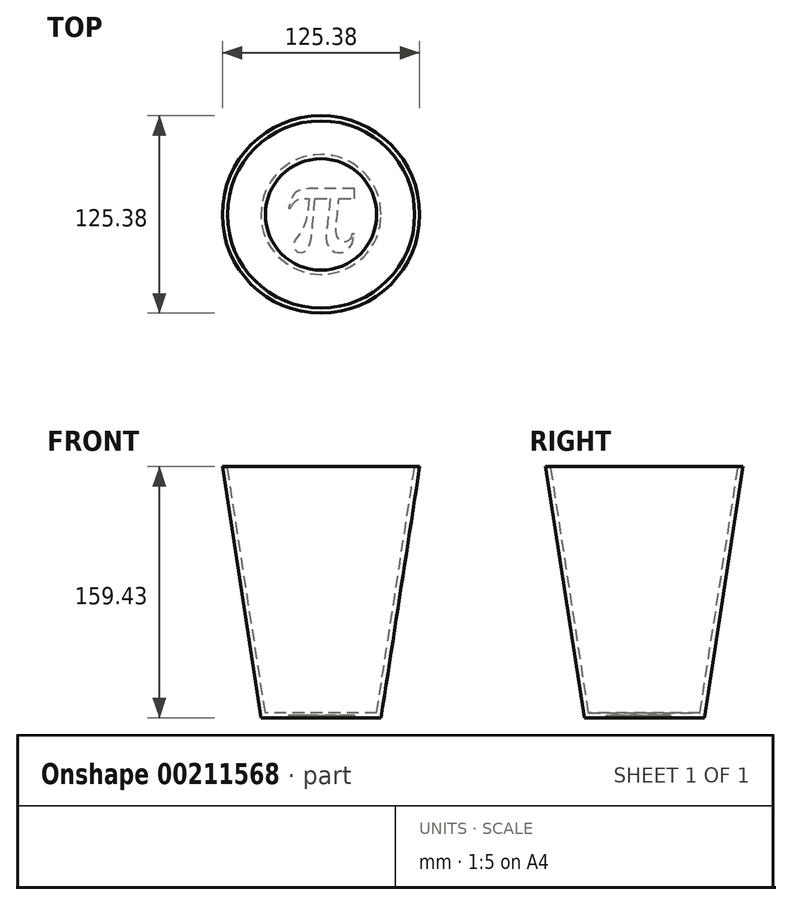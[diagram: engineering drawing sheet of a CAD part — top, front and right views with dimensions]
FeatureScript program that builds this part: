
annotation { "Feature Type Name" : "Feature", "Feature Type Description" : "" }
export const myFeature = defineFeature(function(context is Context, id is Id, definition is map)
    precondition{}
    {
        {
            var Q0;
            Q0=qCreatedBy(makeId("Front.planeOp"),FACE);
            var sketch = newSketch(context, id + "F0", { "sketchPlane" : qUnion([Q0])});
            skLineSegment(sketch, "E0", {"start": v(0, 0) * mm, "end": v(-38.1, 0) * mm});
            skLineSegment(sketch, "E1", {"start": v(-38.1, 0) * mm, "end": v(-62.69, 159.43) * mm});
            skLineSegment(sketch, "E2", {"start": v(-62.69, 159.43) * mm, "end": v(0, 159.43) * mm});
            skLineSegment(sketch, "E3", {"start": v(0, 159.43) * mm, "end": v(0, 0) * mm});
            skSolve(sketch);
        }
        {
            var Q0;
            Q0=makeQuery(id+"F0.imprint","IMPRINT",FACE,{"disambiguationData":[TD([[makeQuery(id+"F0.imprint","IMPRINT",EDGE,{"derivedFrom":sQuery(id+"F0.wireOp",EDGE,"E0")}),-1.0]])]});
            var Q1;
            Q1=sQuery(id+"F0.wireOp",EDGE,"E3");
            revolve(context, id + "F1", {"entities" : qUnion([Q0]), "axis" : qUnion([Q1]), "revolveType" : RevolveType.FULL});
        }
        {
            var Q0;
            Q0=makeQuery(id+"F1.opRevolve","SWEPT_FACE",FACE,{"disambiguationData":[OSD([sQuery(id+"F0.wireOp",EDGE,"E2")])]});
            shell(context, id + "F2", {"entities" : qUnion([Q0]), "thickness" : 3.17 * mm});
        }
        {
            var Q0;
            Q0=qCreatedBy(makeId("Top.planeOp"),FACE);
            var sketch = newSketch(context, id + "F3", { "sketchPlane" : qUnion([Q0])});
            skFitSpline(sketch, "E4", {"points": [v(-7.8, 10.01) * mm, v(-8.3, 3.24) * mm, v(-9.79, -4.43) * mm, v(-13.46, -12.39) * mm, v(-17.05, -17.3) * mm, v(-17.29, -20.76) * mm, v(-16.34, -22.58) * mm, v(-14.8, -23.72) * mm, v(-12.98, -24.13) * mm, v(-10.69, -23.7) * mm, v(-8.8, -22.17) * mm, v(-6.61, -16.96) * mm, v(-5.43, -7.76) * mm, v(-3.85, 10.05) * mm], "startDerivative": vector(-4.12, -76.18) * mm, "endDerivative": vector(12.24, 134.37) * mm});
            skFitSpline(sketch, "E5", {"points": [v(-3.85, 10.05) * mm, v(5.63, 10.05) * mm], "startDerivative": vector(9.49, 0) * mm, "endDerivative": vector(9.49, 0) * mm});
            skFitSpline(sketch, "E6", {"points": [v(5.63, 10.05) * mm, v(3.92, -6.57) * mm, v(3.42, -17.34) * mm, v(6.56, -22.55) * mm, v(9.77, -24.05) * mm, v(12.84, -24.05) * mm, v(14.98, -23.55) * mm, v(18.62, -20.34) * mm, v(20.33, -16.56) * mm, v(21.12, -12.28) * mm, v(21.12, -12.28) * mm], "startDerivative": vector(-8.09, -90.01) * mm, "endDerivative": vector(0.5, -0.57) * mm});
            skFitSpline(sketch, "E7", {"points": [v(21.12, -12.28) * mm, v(19.57, -12.28) * mm, v(19.55, -12.28) * mm], "startDerivative": vector(-2.4, 0) * mm, "endDerivative": vector(-0.1, 0) * mm});
            skFitSpline(sketch, "E8", {"points": [v(19.57, -12.28) * mm, v(18.7, -15.13) * mm, v(16.04, -17.23) * mm, v(13.5, -17.17) * mm, v(10.72, -14.9) * mm, v(9.59, -8.62) * mm, v(10.5, 0.95) * mm, v(11.44, 10.05) * mm], "startDerivative": vector(-4.12, -27) * mm, "endDerivative": vector(4.4, 46.61) * mm});
            skFitSpline(sketch, "E9", {"points": [v(11.44, 10.05) * mm, v(21.12, 10.05) * mm], "startDerivative": vector(9.68, 0) * mm, "endDerivative": vector(9.68, 0) * mm});
            skFitSpline(sketch, "E10", {"points": [v(21.12, 10.05) * mm, v(21.12, 16.43) * mm], "startDerivative": vector(0, 6.37) * mm, "endDerivative": vector(0, 6.37) * mm});
            skFitSpline(sketch, "E11", {"points": [v(21.12, 16.43) * mm, v(-6.08, 16.43) * mm, v(-13.46, 15.41) * mm, v(-17.2, 12.95) * mm, v(-19.06, 8.8) * mm, v(-20.76, 4.21) * mm], "startDerivative": vector(-86.58, 0.98) * mm, "endDerivative": vector(-11.45, -29.7) * mm});
            skFitSpline(sketch, "E12", {"points": [v(-20.76, 4.21) * mm, v(-19.4, 4.21) * mm], "startDerivative": vector(1.36, 0) * mm, "endDerivative": vector(1.36, 0) * mm});
            skFitSpline(sketch, "E13", {"points": [v(-19.4, 4.21) * mm, v(-17.03, 7.77) * mm, v(-12.53, 10.05) * mm, v(-7.8, 10.01) * mm], "startDerivative": vector(6.1, 11.92) * mm, "endDerivative": vector(14.04, -1.57) * mm});
            skSolve(sketch);
        }
        {
            var Q0;
            Q0=makeQuery(id+"F3.imprint","IMPRINT",FACE,{"disambiguationData":[TD([[makeQuery(id+"F3.imprint","IMPRINT",EDGE,{"derivedFrom":sQuery(id+"F3.wireOp",EDGE,"E4")}),1.0]])]});
            extrude(context, id + "F4", {"entities" : qUnion([Q0]), "operationType" : NewBodyOperationType.REMOVE, "depth" : 1.59 * mm});
        }
    });
